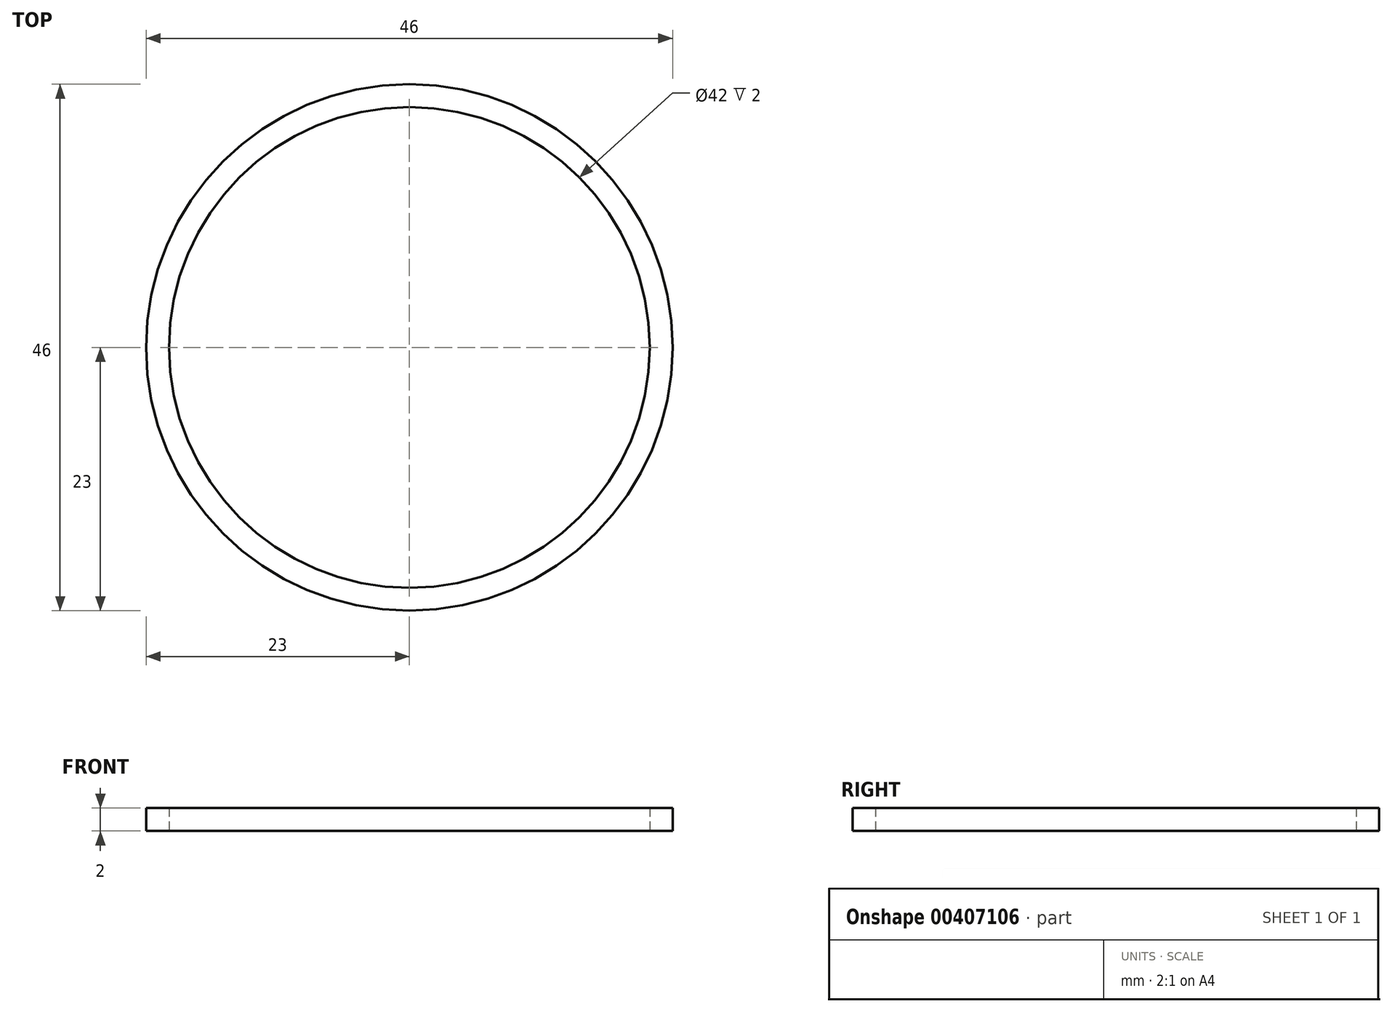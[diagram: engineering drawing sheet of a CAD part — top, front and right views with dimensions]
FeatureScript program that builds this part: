
annotation { "Feature Type Name" : "Feature", "Feature Type Description" : "" }
export const myFeature = defineFeature(function(context is Context, id is Id, definition is map)
    precondition{}
    {
        {
            var Q0;
            Q0=qCreatedBy(makeId("Top.planeOp"),FACE);
            var sketch = newSketch(context, id + "F0", { "sketchPlane" : qUnion([Q0])});
            skCircle(sketch, "E0", {"center": v(0, 0) * mm, "radius": 21 * mm});
            skCircle(sketch, "E1", {"center": v(0, 0) * mm, "radius": 23 * mm});
            skSolve(sketch);
        }
        {
            var Q0;
            Q0=makeQuery(id+"F0.imprint","IMPRINT",FACE,{"disambiguationData":[TD([[makeQuery(id+"F0.imprint","IMPRINT",EDGE,{"derivedFrom":sQuery(id+"F0.wireOp",EDGE,"E0")}),-1.0]])]});
            extrude(context, id + "F1", {"entities" : qUnion([Q0]), "depth" : 2 * mm});
        }
    });
